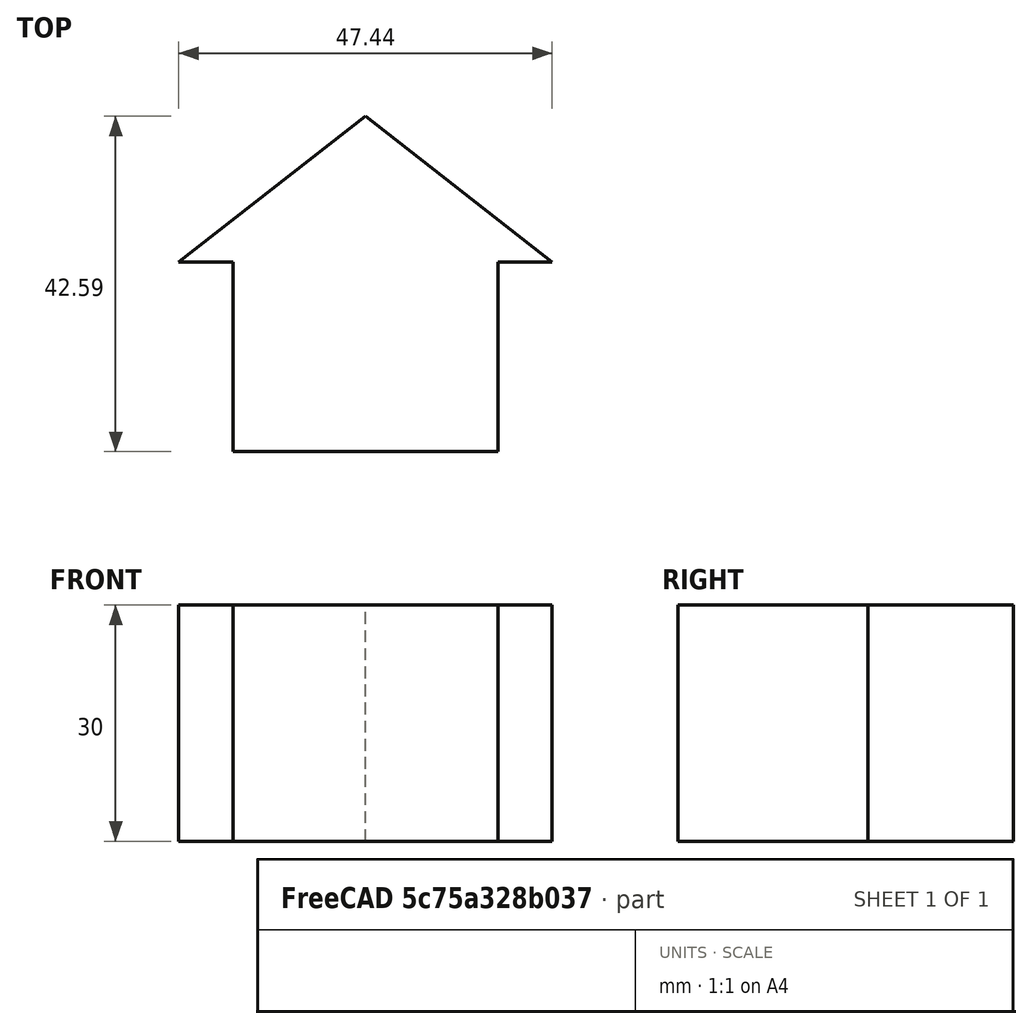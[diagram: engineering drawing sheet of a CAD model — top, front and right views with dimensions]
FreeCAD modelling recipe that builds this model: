
FCSTD DOCUMENT  (FreeCAD 0.16R6705 (Git))
Label: casetta
License: All rights reserved
LicenseURL: http://it.wikipedia.org/wiki/<copyright redacted>
objects: Sketcher::SketchObject×2, PartDesign::Pad×1
note: 4 computed .brp shape members not serialized (recipe doc carries the construction recipe); baked Part::Feature solids carry a one-line shape summary decoded from their .brp

FEATURE [Sketcher::SketchObject] Sketch
  sketch-geometry (7):
    g0: LineSegment StartX=-16.8341 StartY=14.0165 StartZ=0 EndX=-16.8341 EndY=-10.0759 EndZ=0
    g1: LineSegment StartX=-16.8341 StartY=-10.0759 StartZ=0 EndX=16.8341 EndY=-10.0759 EndZ=0
    g2: LineSegment StartX=16.8341 StartY=-10.0759 StartZ=0 EndX=16.8341 EndY=14.0165 EndZ=0
    g3: LineSegment StartX=16.8341 StartY=14.0165 StartZ=0 EndX=23.7223 EndY=14.0165 EndZ=0
    g4: LineSegment StartX=23.7223 StartY=14.0165 StartZ=0 EndX=0 EndY=32.5075 EndZ=0
    g5: LineSegment StartX=0 StartY=32.5075 StartZ=0 EndX=-23.7223 EndY=14.0165 EndZ=0
    g6: LineSegment StartX=-23.7223 StartY=14.0165 StartZ=0 EndX=-16.8341 EndY=14.0165 EndZ=0
  constraints (15):
    c: Coincident(g0,g1)
    c: Coincident(g1,g2)
    c: Coincident(g2,g3)
    c: Coincident(g3,g4)
    c: Coincident(g4,g5)
    c: Coincident(g5,g6)
    c: Coincident(g0,g6)
    c: Equal(g6,g3)
    c: Horizontal(g6)
    c: Horizontal(g3)
    c: Equal(g2,g0)
    c: Equal(g5,g4)
    c: Symmetric(g2,g0,g-2)
    c: Vertical(g0)
    c: Vertical(g2)
FEATURE [PartDesign::Pad] Pad
  Length = 30
  Length2 = 100
  Sketch = -> Sketch
  Type = 0
FEATURE [Sketcher::SketchObject] Sketch001
  ExternalGeometry = -> [Pad]
  Placement = pos=(0,0,30) rot=(0,0,1;0rad)
  Support = -> Pad [Face9]
  sketch-geometry (3):
    g0: LineSegment StartX=0 StartY=32.5075 StartZ=0 EndX=0 EndY=14.0165 EndZ=0
    g1: LineSegment StartX=0 StartY=14.0165 StartZ=0 EndX=23.7223 EndY=14.0165 EndZ=0
    g2: LineSegment StartX=0 StartY=32.5075 StartZ=0 EndX=23.7223 EndY=14.0165 EndZ=0
  constraints (7):
    c: Coincident(g-3,g0)
    c: Coincident(g0,g2)
    c: Coincident(g1,g2)
    c: Coincident(g0,g1)
    c: Coincident(g-4,g1)
    c: PointOnObject(g0,g-2)
    c: Horizontal(g1)
